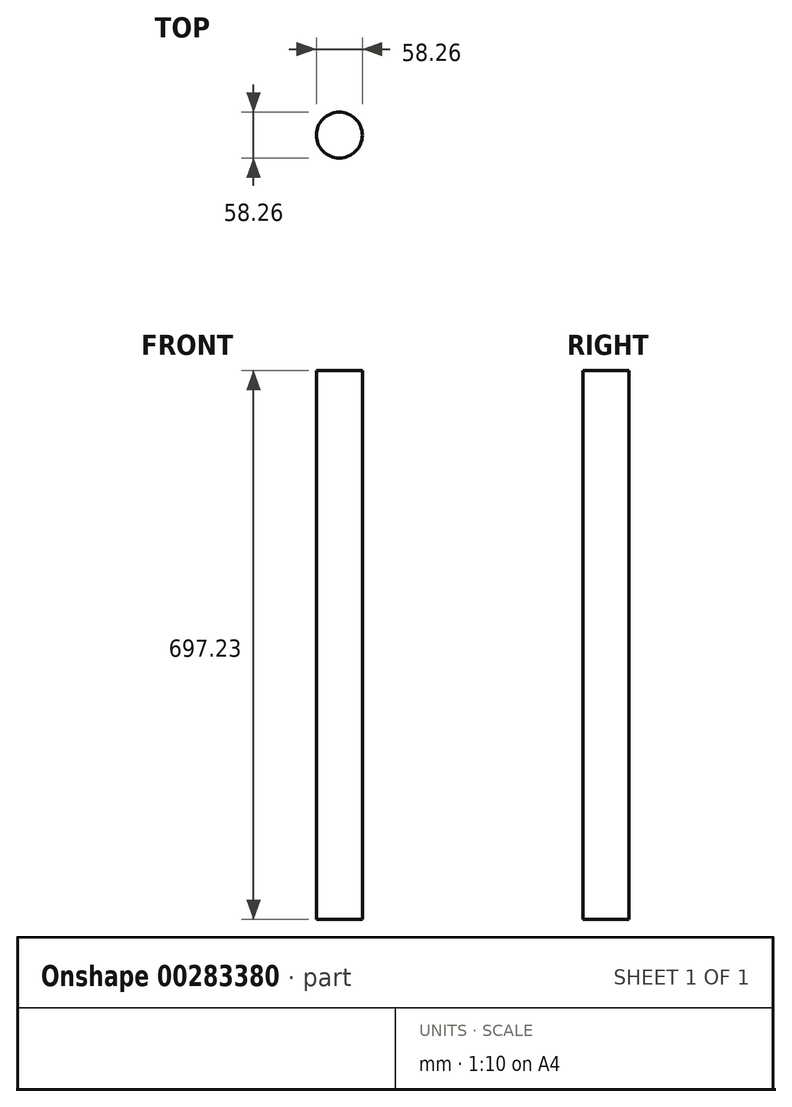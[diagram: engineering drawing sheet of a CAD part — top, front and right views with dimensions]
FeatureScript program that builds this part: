
annotation { "Feature Type Name" : "Feature", "Feature Type Description" : "" }
export const myFeature = defineFeature(function(context is Context, id is Id, definition is map)
    precondition{}
    {
        {
            var Q0;
            Q0=qCreatedBy(makeId("Top.planeOp"),FACE);
            var sketch = newSketch(context, id + "F0", { "sketchPlane" : qUnion([Q0])});
            skCircle(sketch, "E0", {"center": v(0, 0) * mm, "radius": 29.13 * mm});
            skSolve(sketch);
        }
        {
            var Q0;
            Q0 = qSketchRegion(id + "F0", true);
            extrude(context, id + "F1", {"entities" : qUnion([Q0]), "depth" : 697.23 * mm});
        }
    });
